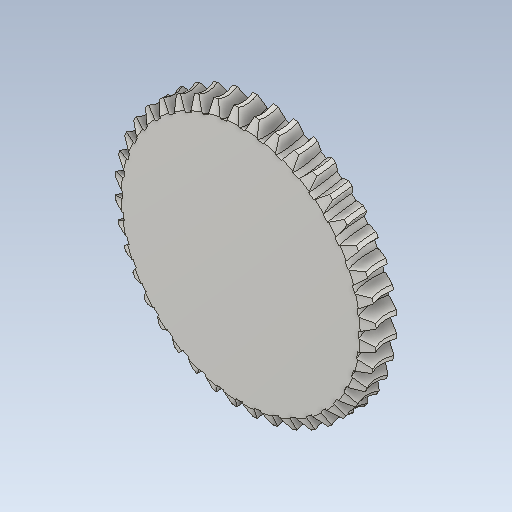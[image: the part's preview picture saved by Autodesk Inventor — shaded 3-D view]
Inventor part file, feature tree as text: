
AUTODESK INVENTOR PART (.ipt)
format: ipt  version: 2020.3 (Build 243373000, 373)  size: 644,608 bytes
history: native  units: mm (DEFAULTED — no unit token found)
features: other x8, plane x3, pattern_circular x1, sketch x1
ambient origin geometry x5: Origin, X Axis, Y Axis, Z Axis, Center Point
bodies: Solid1 (feature_tree)
feature tree (13):
  other  "Tooth Plane"
  other  "Base Body Sketch"
  other  "Base Body"
  other  "Base Body2"
  plane  "Work Plane13"
  other  "Tooth"
  pattern_circular  "Tooth Pattern"  [2 undecoded]
  plane  "Work Plane14"
  plane  "Work Plane15"
  other  "Tooth Sketch"
  sketch  "Sketch8"  dims[d35=90.0deg d37=-0.996687mm d38=63.164618mm d39=3.490659mm d40=9.601022mm d41=12.632924mm d42=2.38125mm d43=90.0deg d44=400.0mm d46=360.0deg d50=4.322105mm d68=63.164618mm d69=0.0mm d73=0.0mm d75=0.785398mm d77=101.063389mm d78=12.7mm d79=0.0mm d80=0.0mm d81=0.0mm d82=0.0mm d83=0.785398mm d84=0.0mm d85=180.0deg d86=63.164618mm d87=108.643143mm d89=20.212678mm d90=90.0deg d92=12.7mm d93=63.164618mm]
  other  "Srf1"
  other  "Pitch Diameter"
note: 2 required parameter values undecoded (feature->parameter linkage not recoverable at this tier; creation-order binding heuristic only, values carry confidence <= 0.55)
